FCSTD DOCUMENT  (FreeCAD 0.17R9284 (Git))
Label: TestTube3
License: All rights reserved
LicenseURL: http://en.wikipedia.org/wiki/All_rights_reserved
objects: Sketcher::SketchObject×1, PartDesign::Body×1
note: 2 computed .brp shape members not serialized (recipe doc carries the construction recipe); baked Part::Feature solids carry a one-line shape summary decoded from their .brp

FEATURE [Sketcher::SketchObject] Sketch
  MapMode = 5
  Placement = pos=(0,0,0) rot=(1,0,0;1.5708rad)
  Support = -> [XZ_Plane]
  expr: Constraints[25] = 150 - 0.5
  sketch-geometry (9):
    g0: LineSegment StartX=-17.5 StartY=65.75 StartZ=0 EndX=-17.5 EndY=-65.75 EndZ=0
    g1: LineSegment [constr] StartX=3e-12 StartY=-65.75 StartZ=0 EndX=-17.5 EndY=-65.75 EndZ=0
    g2: ArcOfCircle CenterX=3e-12 CenterY=-65.75 CenterZ=0 NormalX=0 NormalY=0 NormalZ=1 Radius=17.5 StartAngle=3.14159 EndAngle=4.71239
    g3: LineSegment [constr] StartX=-17.5 StartY=65.75 StartZ=0 EndX=-17.5 EndY=66.25 EndZ=0
    g4: LineSegment [constr] StartX=-17.5 StartY=66.25 StartZ=0 EndX=-17 EndY=66.25 EndZ=0
    g5: ArcOfCircle CenterX=-17.5 CenterY=66.25 CenterZ=0 NormalX=0 NormalY=0 NormalZ=1 Radius=0.5 StartAngle=-2.3e-11 EndAngle=4.71239
    g6: LineSegment StartX=-17 StartY=66.25 StartZ=0 EndX=-17 EndY=-65.75 EndZ=0
    g7: ArcOfCircle CenterX=3e-12 CenterY=-65.75 CenterZ=0 NormalX=0 NormalY=0 NormalZ=1 Radius=17 StartAngle=3.14159 EndAngle=4.71239
    g8: LineSegment StartX=4e-12 StartY=-82.75 StartZ=0 EndX=-7e-12 EndY=-83.25 EndZ=0
  constraints (27):
    c: Vertical(g0)
    c: PointOnObject(g1,g-2)
    c: Coincident(g1,g0)
    c: Horizontal(g1)
    c: Coincident(g2,g1)
    c: Coincident(g2,g0)
    c: PointOnObject(g2,g-2)
    c: Coincident(g3,g0)
    c: Vertical(g3)
    c: Coincident(g4,g3)
    c: Horizontal(g4)
    c: Coincident(g5,g3)
    c: Coincident(g5,g0)
    c: PointOnObject(g5,g4)
    c: Coincident(g4,g5)
    c: Coincident(g6,g4)
    c: PointOnObject(g6,g1)
    c: Vertical(g6)
    c: Coincident(g7,g1)
    c: Coincident(g7,g6)
    c: PointOnObject(g7,g-2)
    c: Coincident(g8,g7)
    c: Coincident(g8,g2)
    c: Symmetric(g0,g0,g-1)
    c: DistanceX(g1,g1) = 17.5
    c: DistanceY(g2,g4) = 149.5
    c: DistanceX(g4,g4) = 0.5
FEATURE [PartDesign::Body] Body
  Model = -> [Sketch]
  Origin = -> BodyOrigin
